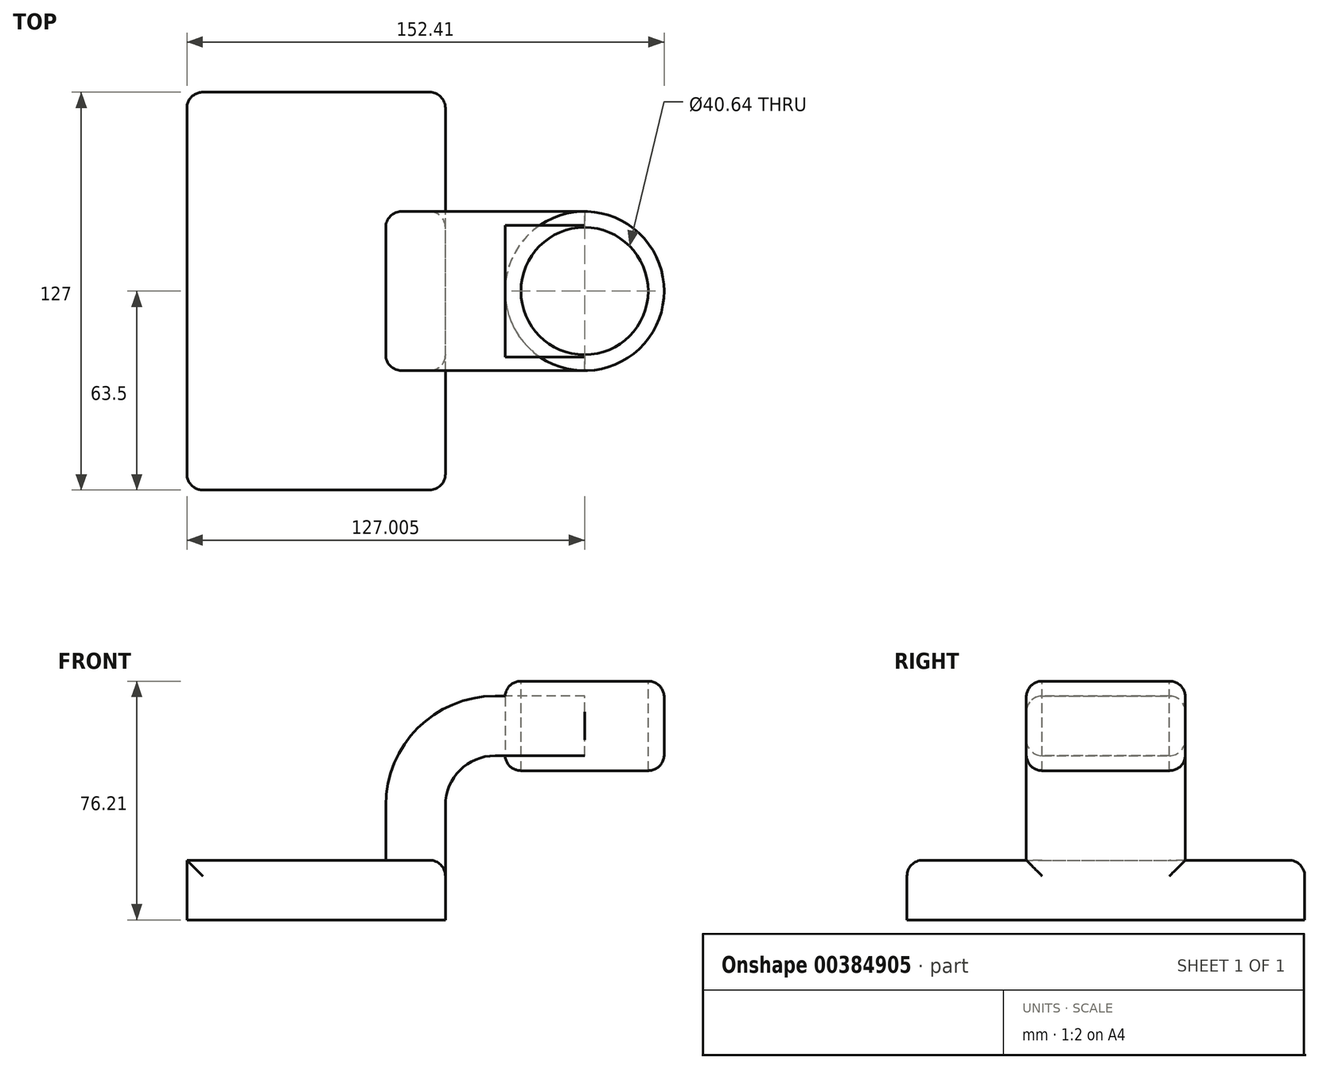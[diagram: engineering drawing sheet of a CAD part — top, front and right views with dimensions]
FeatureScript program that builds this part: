
annotation { "Feature Type Name" : "Feature", "Feature Type Description" : "" }
export const myFeature = defineFeature(function(context is Context, id is Id, definition is map)
    precondition{}
    {
        {
            var Q0;
            Q0=qCreatedBy(makeId("Front.planeOp"),FACE);
            var sketch = newSketch(context, id + "F0", { "sketchPlane" : qUnion([Q0])});
            skLineSegment(sketch, "E0.bottom", {"start": v(-41.28, -9.53) * mm, "end": v(41.28, -9.53) * mm});
            skLineSegment(sketch, "E0.top", {"start": v(-41.28, 9.52) * mm, "end": v(41.28, 9.52) * mm});
            skLineSegment(sketch, "E0.left", {"start": v(-41.28, -9.53) * mm, "end": v(-41.28, 9.52) * mm});
            skLineSegment(sketch, "E0.right", {"start": v(41.28, -9.53) * mm, "end": v(41.28, 9.52) * mm});
            skPoint(sketch, "E0.middle", {"position": v(0, 0) * mm});
            skLineSegment(sketch, "E1.bottom", {"start": v(60.32, 38.1) * mm, "end": v(111.12, 38.1) * mm});
            skLineSegment(sketch, "E1.top", {"start": v(60.32, 66.68) * mm, "end": v(111.12, 66.68) * mm});
            skLineSegment(sketch, "E1.left", {"start": v(60.32, 38.1) * mm, "end": v(60.32, 66.67) * mm});
            skLineSegment(sketch, "E1.right", {"start": v(111.12, 38.1) * mm, "end": v(111.12, 66.67) * mm});
            skPoint(sketch, "E1.middle", {"position": v(85.72, 52.39) * mm});
            skLineSegment(sketch, "E2", {"start": v(41.27, 9.52) * mm, "end": v(41.27, 27) * mm});
            skArc(sketch, "E3", {"start": v(41.27, 27) * mm, "mid": v(45.92, 38.23) * mm, "end": v(57.15, 42.88) * mm});
            skLineSegment(sketch, "E4", {"start": v(57.15, 42.88) * mm, "end": v(85.72, 42.88) * mm});
            skLineSegment(sketch, "E5.0", {"start": v(57.15, 61.93) * mm, "end": v(85.72, 61.93) * mm});
            skArc(sketch, "E5.1", {"start": v(22.22, 27) * mm, "mid": v(32.45, 51.7) * mm, "end": v(57.15, 61.93) * mm});
            skLineSegment(sketch, "E5.2", {"start": v(22.22, 9.52) * mm, "end": v(22.22, 27) * mm});
            skLineSegment(sketch, "E6.0", {"start": v(57.15, 61.88) * mm, "end": v(85.72, 61.88) * mm});
            skLineSegment(sketch, "E7", {"start": v(85.72, 38.1) * mm, "end": v(85.72, 66.68) * mm});
            skFitSpline(sketch, "E8", {"points": [v(-41.28, 9.53) * mm, v(57.15, 61.93) * mm], "startDerivative": vector(20.13, 70.75) * mm, "endDerivative": vector(150, -7.04) * mm});
            skSolve(sketch);
        }
        {
            var Q0;
            Q0=makeQuery(id+"F0.imprint","IMPRINT",FACE,{"disambiguationData":[TD([[makeQuery(id+"F0.imprint","IMPRINT",EDGE,{"derivedFrom":sQuery(id+"F0.wireOp",EDGE,"E0.bottom")}),1.0]])]});
            extrude(context, id + "F1", {"entities" : qUnion([Q0]), "endBound" : BoundingType.SYMMETRIC, "depth" : 127 * mm});
        }
        {
            var Q0;
            {var subQ0=sQuery(id+"F0.wireOp",EDGE,"E2");Q0=makeQuery(id+"F0.imprint","IMPRINT",FACE,{"disambiguationData":[TD([[makeQuery(id+"F0.imprint","IMPRINT",EDGE,{"derivedFrom":subQ0}),1.0]])]});}
            extrude(context, id + "F2", {"entities" : qUnion([Q0]), "operationType" : NewBodyOperationType.ADD, "endBound" : BoundingType.SYMMETRIC, "depth" : 50.8 * mm});
        }
        {
            var Q0;
            Q0=makeQuery(id+"F0.imprint","IMPRINT",FACE,{"disambiguationData":[TD([[makeQuery(id+"F0.imprint","IMPRINT",EDGE,{"derivedFrom":sQuery(id+"F0.wireOp",EDGE,"E5.1")}),1.0]])]});
            extrude(context, id + "F3", {"entities" : qUnion([Q0]), "operationType" : NewBodyOperationType.ADD, "endBound" : BoundingType.SYMMETRIC, "depth" : 15.88 * mm});
        }
        {
            var Q0;
            {var subQ0=sQuery(id+"F0.wireOp",EDGE,"E4");var subQ1=sQuery(id+"F0.wireOp",EDGE,"E1.left");var subQ2=makeQuery(id+"F0.imprint","INTERSECT",VERTEX,{"derivedFrom":[subQ1,subQ0]});Q0=makeQuery(id+"F0.imprint","IMPRINT",FACE,{"disambiguationData":[TD([[makeQuery(id+"F0.imprint","IMPRINT",EDGE,{"disambiguationData":[TD([[subQ2,-1.0]])],"derivedFrom":subQ1}),-1.0]])]});}
            extrude(context, id + "F4", {"entities" : qUnion([Q0]), "operationType" : NewBodyOperationType.ADD, "endBound" : BoundingType.SYMMETRIC, "depth" : 50.8 * mm});
        }
        {
            var Q0;
            {var subQ4=sQuery(id+"F0.wireOp",EDGE,"E1.right");Q0=makeQuery(id+"F0.imprint","IMPRINT",FACE,{"disambiguationData":[TD([[makeQuery(id+"F0.imprint","IMPRINT",EDGE,{"derivedFrom":subQ4}),1.0]])]});}
            var Q1;
            Q1=sQuery(id+"F0.wireOp",EDGE,"E7");
            revolve(context, id + "F5", {"entities" : qUnion([Q0]), "axis" : qUnion([Q1]), "revolveType" : RevolveType.FULL});
        }
        {
            var Q0;
            Q0=makeQuery(id+"F1.opExtrude","CAP_EDGE",EDGE,{"disambiguationData":[OSD([sQuery(id+"F0.wireOp",EDGE,"E0.right")])],"isStart":false});
            var Q1;
            Q1=makeQuery(id+"F1.opExtrude","CAP_EDGE",EDGE,{"disambiguationData":[OSD([sQuery(id+"F0.wireOp",EDGE,"E0.left")])],"isStart":false});
            var Q2;
            Q2=makeQuery(id+"F1.opExtrude","CAP_EDGE",EDGE,{"disambiguationData":[OSD([sQuery(id+"F0.wireOp",EDGE,"E0.right")])],"isStart":true});
            var Q3;
            Q3=makeQuery(id+"F1.opExtrude","CAP_EDGE",EDGE,{"disambiguationData":[OSD([sQuery(id+"F0.wireOp",EDGE,"E0.left")])],"isStart":true});
            var Q4;
            Q4=makeQuery(id+"F2.opExtrude","CAP_EDGE",EDGE,{"disambiguationData":[OSD([sQuery(id+"F0.wireOp",EDGE,"E3")])],"isStart":false});
            var Q5;
            Q5=makeQuery(id+"F2.opExtrude","CAP_EDGE",EDGE,{"disambiguationData":[OSD([sQuery(id+"F0.wireOp",EDGE,"E3")])],"isStart":true});
            var Q6;
            Q6=makeQuery(id+"F2.opExtrude","CAP_EDGE",EDGE,{"disambiguationData":[OSD([sQuery(id+"F0.wireOp",EDGE,"E5.1")])],"isStart":false});
            var Q7;
            Q7=makeQuery(id+"F2.opExtrude","CAP_EDGE",EDGE,{"disambiguationData":[OSD([sQuery(id+"F0.wireOp",EDGE,"E5.1")])],"isStart":true});
            var Q8;
            Q8=makeQuery(id+"F5.opRevolve","SWEPT_EDGE",EDGE,{"disambiguationData":[OSD([sQuery(id+"F0.wireOp",EDGE,"E1.top"),sQuery(id+"F0.wireOp",EDGE,"E1.right")])]});
            var Q9;
            Q9=makeQuery(id+"F5.opRevolve","SWEPT_EDGE",EDGE,{"disambiguationData":[OSD([sQuery(id+"F0.wireOp",EDGE,"E1.bottom"),sQuery(id+"F0.wireOp",EDGE,"E1.right")])]});
            var Q10;
            Q10=makeQuery(id+"F3.opExtrude","CAP_EDGE",EDGE,{"disambiguationData":[OSD([sQuery(id+"F0.wireOp",EDGE,"E8")])],"isStart":false});
            var Q11;
            Q11=makeQuery(id+"F3.opExtrude","CAP_EDGE",EDGE,{"disambiguationData":[OSD([sQuery(id+"F0.wireOp",EDGE,"E8")])],"isStart":true});
            var Q12;
            Q12=makeQuery(id+"F1.opExtrude","CAP_EDGE",EDGE,{"disambiguationData":[OSD([sQuery(id+"F0.wireOp",EDGE,"E0.top")])],"isStart":false});
            var Q13;
            {var subQ0=sQuery(id+"F0.wireOp",EDGE,"E0.right");var subQ1=sQuery(id+"F0.wireOp",EDGE,"E2");var subQ2=sQuery(id+"F0.wireOp",EDGE,"E0.top");Q13=makeQuery(id+"F2.boolean.opBoolean","SPLIT",EDGE,{"disambiguationData":[TD([makeQuery(id+"F1.opExtrude","CAP_FACE",FACE,{"disambiguationData":[OSD([sQuery(id+"F0.wireOp",EDGE,"E0.bottom"),subQ2,sQuery(id+"F0.wireOp",EDGE,"E0.left"),subQ0])],"isStart":false})])],"derivedFrom":makeQuery(id+"F1.opExtrude","SWEPT_EDGE",EDGE,{"disambiguationData":[OSD([subQ2,subQ0,subQ1])]})});}
            var Q14;
            {var subQ0=sQuery(id+"F0.wireOp",EDGE,"E2");var subQ1=sQuery(id+"F0.wireOp",EDGE,"E0.top");var subQ2=sQuery(id+"F0.wireOp",EDGE,"E0.right");Q14=makeQuery(id+"F2.boolean.opBoolean","SPLIT",EDGE,{"disambiguationData":[TD([makeQuery(id+"F1.opExtrude","CAP_FACE",FACE,{"disambiguationData":[OSD([sQuery(id+"F0.wireOp",EDGE,"E0.bottom"),subQ1,sQuery(id+"F0.wireOp",EDGE,"E0.left"),subQ2])],"isStart":true})])],"derivedFrom":makeQuery(id+"F1.opExtrude","SWEPT_EDGE",EDGE,{"disambiguationData":[OSD([subQ1,subQ2,subQ0])]})});}
            var Q15;
            Q15=makeQuery(id+"F1.opExtrude","CAP_EDGE",EDGE,{"disambiguationData":[OSD([sQuery(id+"F0.wireOp",EDGE,"E0.top")])],"isStart":true});
            fillet(context, id + "F6", {"entities" : qUnion([Q0, Q1, Q2, Q3, Q4, Q5, Q6, Q7, Q8, Q9, Q10, Q11, Q12, Q13, Q14, Q15]), "radius" : 5.08 * mm, "tangentPropagation" : true, "allowEdgeOverflow" : false});
        }
        {
            var Q0;
            Q0=makeQuery(id+"F5.opRevolve","SWEPT_FACE",FACE,{"disambiguationData":[OSD([sQuery(id+"F0.wireOp",EDGE,"E1.top")])]});
            extrude(context, id + "F7", {"entities" : qUnion([Q0]), "operationType" : NewBodyOperationType.REMOVE, "endBound" : BoundingType.THROUGH_ALL, "oppositeDirection" : true, "depth" : 25.4 * mm});
        }
    });
